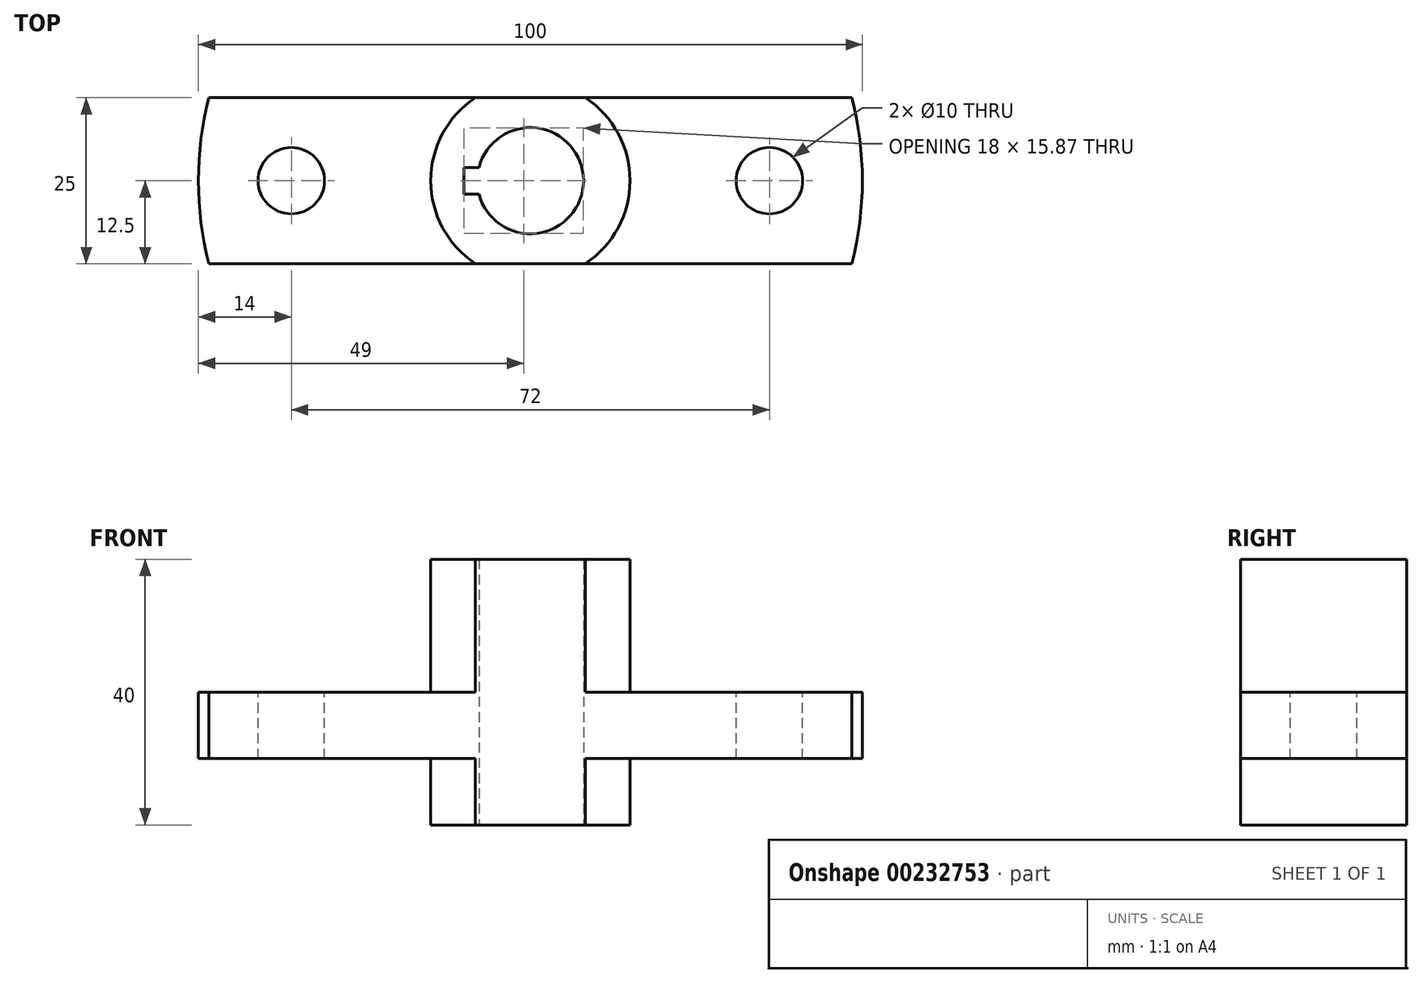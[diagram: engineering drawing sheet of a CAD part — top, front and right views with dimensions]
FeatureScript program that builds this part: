
annotation { "Feature Type Name" : "Feature", "Feature Type Description" : "" }
export const myFeature = defineFeature(function(context is Context, id is Id, definition is map)
    precondition{}
    {
        {
            var Q0;
            Q0=qCreatedBy(makeId("Top.planeOp"),FACE);
            var sketch = newSketch(context, id + "F0", { "sketchPlane" : qUnion([Q0])});
            skArc(sketch, "E0", {"start": v(-48.41, 12.5) * mm, "mid": v(-50, 0) * mm, "end": v(-48.41, -12.5) * mm});
            skArc(sketch, "E1", {"start": v(-7.75, -2) * mm, "mid": v(8, 0) * mm, "end": v(-7.75, 2) * mm});
            skArc(sketch, "E2", {"start": v(-8.3, 12.5) * mm, "mid": v(-15, 0) * mm, "end": v(-8.3, -12.5) * mm});
            skLineSegment(sketch, "E3.bottom", {"start": v(-48.41, 12.5) * mm, "end": v(48.41, 12.5) * mm});
            skLineSegment(sketch, "E3.top", {"start": v(-48.41, -12.5) * mm, "end": v(48.41, -12.5) * mm});
            skArc(sketch, "E4.trimOffspring", {"start": v(48.41, -12.5) * mm, "mid": v(50, 0) * mm, "end": v(48.41, 12.5) * mm});
            skArc(sketch, "E5.trimOffspring", {"start": v(8.3, -12.5) * mm, "mid": v(15, 0) * mm, "end": v(8.3, 12.5) * mm});
            skLineSegment(sketch, "E6.bottom", {"start": v(-7.75, -2) * mm, "end": v(-10, -2) * mm});
            skLineSegment(sketch, "E6.top", {"start": v(-7.75, 2) * mm, "end": v(-10, 2) * mm});
            skLineSegment(sketch, "E6.right", {"start": v(-10, -2) * mm, "end": v(-10, 2) * mm});
            skPoint(sketch, "E6.middle", {"position": v(-8, 0) * mm});
            skPoint(sketch, "E6.left.end.orphan", {"position": v(-6, 2) * mm});
            skPoint(sketch, "E7.orphan", {"position": v(-6, -2) * mm});
            skCircle(sketch, "E8", {"center": v(-36, 0) * mm, "radius": 5 * mm});
            skCircle(sketch, "E9", {"center": v(36, 0) * mm, "radius": 5 * mm});
            skSolve(sketch);
        }
        {
            var Q0;
            Q0=makeQuery(id+"F0.imprint","IMPRINT",FACE,{"disambiguationData":[TD([[makeQuery(id+"F0.imprint","IMPRINT",EDGE,{"derivedFrom":sQuery(id+"F0.wireOp",EDGE,"E1")}),-1.0]])]});
            extrude(context, id + "F1", {"entities" : qUnion([Q0]), "depth" : 20 * mm, "hasSecondDirection" : true, "secondDirectionOppositeDirection" : true, "secondDirectionDepth" : 20 * mm});
        }
        {
            var Q0;
            {var subQ1=sQuery(id+"F0.wireOp",EDGE,"E0");Q0=makeQuery(id+"F0.imprint","IMPRINT",FACE,{"disambiguationData":[TD([[makeQuery(id+"F0.imprint","IMPRINT",EDGE,{"derivedFrom":subQ1}),1.0]])]});}
            var Q1;
            {var subQ1=sQuery(id+"F0.wireOp",EDGE,"E4.trimOffspring");Q1=makeQuery(id+"F0.imprint","IMPRINT",FACE,{"disambiguationData":[TD([[makeQuery(id+"F0.imprint","IMPRINT",EDGE,{"derivedFrom":subQ1}),1.0]])]});}
            extrude(context, id + "F2", {"entities" : qUnion([Q0, Q1]), "operationType" : NewBodyOperationType.ADD, "oppositeDirection" : true, "depth" : 10 * mm});
        }
    });
